# Revit family: Lighting_Fixture-Wall-Astro-Parma100
name_source: partatom
category: Lighting Fixtures
revit_build: Autodesk Revit 2018 (Build: 20170223_1515(x64)
units: mm (PartAtom-declared; Revit-internal decimal feet)

## family parameters
Cut with Voids When Loaded = No
Host = Face
Light Source = Yes
OmniClass Number = 23.80.70.00
OmniClass Title = Lighting
Part Type = Normal
Room Calculation Point = No
Round Connector Dimension = Use Diameter
Shared = No

## types (1)
- Type 1
    Apparent Load = 4 VA
    Casing Material = Astro - Plaster - Natural
    Class = 1
    Color Filter = 16777215
    Description = Wall Light
    Dimmable = No
    Dimming Lamp Color Temperature Shift = <None>
    Energy Efficiency Rating = -
    Heatsink Material = Astro - Aluminium - Anodised
    Height = 100 mm  [stored 0.328084 ft]
    IP Rating = IP20
    Lamp = LED
    Lamp included = Yes
    Length = 100 mm  [stored 0.328084 ft]
    Light Source Elevation = 1590 mm  [stored 5.21654 ft]
    Light Source From Wall = 80 mm  [stored 0.262467 ft]
    Luminaire Lamp Efficiency Rating = -
    Manufacturer = Astro Lighting Ltd, CM20 2DP
    Model = 7019 Parma 100
    Mountable on normally flammable surfaces = Yes
    Number of Poles = 1
    Photometric Web File = 7019 PARMA SINGLE.ies
    Product Documentation = http://www.astrolighting.co.uk
/kw/7019/7019_Parma-100
    Suitable for bathroom zone = Zone 3
    Tilt Angle = -90.00°
    Type Comments = Includes LED driver
    URL = http://www.astrolighting.co.uk
    Voltage = 230 V
    Wattage Comments = 3w
    Weight = 0.75 kg
    Width = 70 mm  [stored 0.229659 ft]

note: [stored X ft] marks values corroborated as IEEE doubles in the binary element streams (Revit-internal decimal feet)

## geometry (parser evidence)
native form markers: Sweep x3
no freeform markers — native parametric forms only
